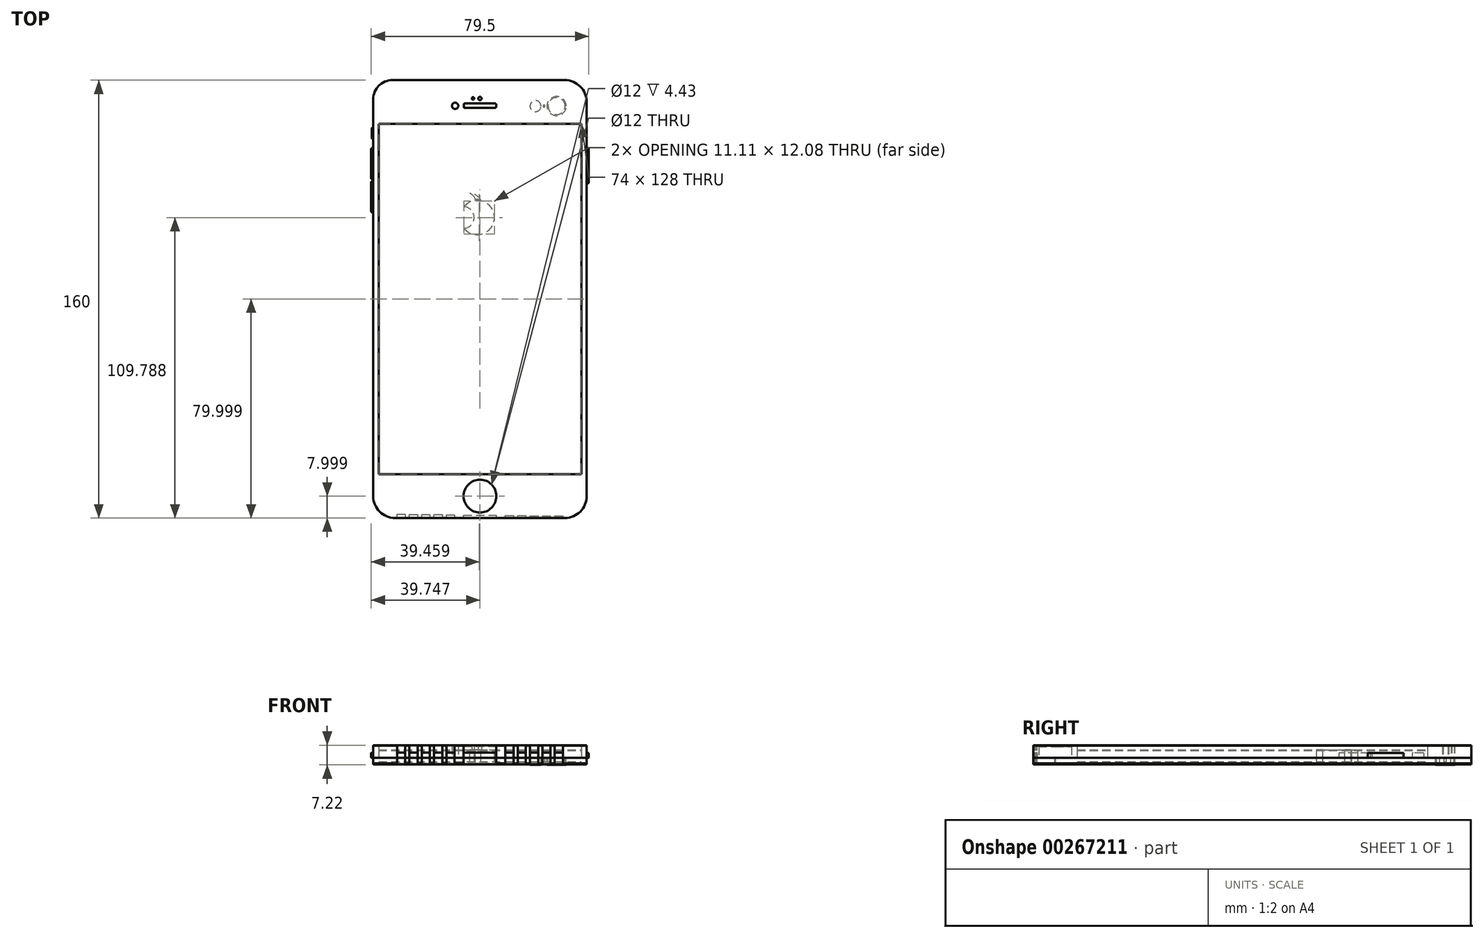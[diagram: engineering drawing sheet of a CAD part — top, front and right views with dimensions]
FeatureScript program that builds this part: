
annotation { "Feature Type Name" : "Feature", "Feature Type Description" : "" }
export const myFeature = defineFeature(function(context is Context, id is Id, definition is map)
    precondition{}
    {
        {
            var Q0;
            Q0=qCreatedBy(makeId("Top.planeOp"),FACE);
            var sketch = newSketch(context, id + "F0", { "sketchPlane" : qUnion([Q0])});
            skLineSegment(sketch, "E0", {"start": v(-50.56, 65.79) * mm, "end": v(-50.56, -79.21) * mm});
            skLineSegment(sketch, "E1", {"start": v(-42.56, -87.21) * mm, "end": v(19.44, -87.21) * mm});
            skLineSegment(sketch, "E2", {"start": v(27.44, -79.21) * mm, "end": v(27.44, 64.79) * mm});
            skLineSegment(sketch, "E3", {"start": v(19.44, 72.79) * mm, "end": v(-43.56, 72.79) * mm});
            skPoint(sketch, "E4.visualSharp", {"position": v(-50.56, 72.79) * mm});
            skArc(sketch, "E4.filletArc", {"start": v(-43.56, 72.79) * mm, "mid": v(-48.51, 70.74) * mm, "end": v(-50.56, 65.79) * mm});
            skPoint(sketch, "E5.visualSharp", {"position": v(27.44, 72.79) * mm});
            skArc(sketch, "E5.filletArc", {"start": v(27.44, 64.79) * mm, "mid": v(25.1, 70.45) * mm, "end": v(19.44, 72.79) * mm});
            skPoint(sketch, "E6.visualSharp", {"position": v(27.44, -87.21) * mm});
            skArc(sketch, "E6.filletArc", {"start": v(19.44, -87.21) * mm, "mid": v(25.1, -84.87) * mm, "end": v(27.44, -79.21) * mm});
            skPoint(sketch, "E7.visualSharp", {"position": v(-50.56, -87.21) * mm});
            skArc(sketch, "E7.filletArc", {"start": v(-50.56, -79.21) * mm, "mid": v(-48.22, -84.87) * mm, "end": v(-42.56, -87.21) * mm});
            skLineSegment(sketch, "E8", {"start": v(-48.56, -71.21) * mm, "end": v(25.44, -71.21) * mm});
            skCircle(sketch, "E9", {"center": v(-11.56, -79.21) * mm, "radius": 6 * mm});
            skLineSegment(sketch, "E10", {"start": v(-48.56, 56.79) * mm, "end": v(25.44, 56.79) * mm});
            skLineSegment(sketch, "E11", {"start": v(-17.49, 63.79) * mm, "end": v(-17.49, 63.1) * mm});
            skLineSegment(sketch, "E12", {"start": v(-16.99, 62.6) * mm, "end": v(-6.14, 62.6) * mm});
            skLineSegment(sketch, "E13", {"start": v(-5.64, 63.1) * mm, "end": v(-5.64, 63.79) * mm});
            skLineSegment(sketch, "E14", {"start": v(-6.14, 64.29) * mm, "end": v(-16.99, 64.29) * mm});
            skCircle(sketch, "E15", {"center": v(-20.64, 63.39) * mm, "radius": 1.15 * mm});
            skPoint(sketch, "E16.visualSharp", {"position": v(-5.64, 62.6) * mm});
            skArc(sketch, "E16.filletArc", {"start": v(-6.14, 62.6) * mm, "mid": v(-5.79, 62.74) * mm, "end": v(-5.64, 63.1) * mm});
            skPoint(sketch, "E17.visualSharp", {"position": v(-5.64, 64.29) * mm});
            skArc(sketch, "E17.filletArc", {"start": v(-5.64, 63.79) * mm, "mid": v(-5.79, 64.14) * mm, "end": v(-6.14, 64.29) * mm});
            skPoint(sketch, "E18.visualSharp", {"position": v(-17.49, 64.29) * mm});
            skArc(sketch, "E18.filletArc", {"start": v(-16.99, 64.29) * mm, "mid": v(-17.34, 64.14) * mm, "end": v(-17.49, 63.79) * mm});
            skPoint(sketch, "E19.visualSharp", {"position": v(-17.49, 62.6) * mm});
            skArc(sketch, "E19.filletArc", {"start": v(-17.49, 63.1) * mm, "mid": v(-17.34, 62.74) * mm, "end": v(-16.99, 62.6) * mm});
            skLineSegment(sketch, "E20", {"start": v(25.44, -71.21) * mm, "end": v(25.44, 56.79) * mm});
            skLineSegment(sketch, "E21", {"start": v(-48.56, 56.79) * mm, "end": v(-48.56, -71.21) * mm});
            skCircle(sketch, "E22", {"center": v(-14.11, 66.09) * mm, "radius": 0.45 * mm});
            skCircle(sketch, "E23", {"center": v(-11.56, 66.09) * mm, "radius": 0.6 * mm});
            skPoint(sketch, "E24.start.orphan", {"position": v(-17.49, 63.44) * mm});
            skPoint(sketch, "E25.center.orphan", {"position": v(9.63, 64.79) * mm});
            skPoint(sketch, "E26.center.orphan", {"position": v(4.38, 64.79) * mm});
            skPoint(sketch, "E27.center.orphan", {"position": v(15.68, 63.79) * mm});
            skPoint(sketch, "E28.center.orphan", {"position": v(4.32, 63.79) * mm});
            skPoint(sketch, "E29.center.orphan", {"position": v(8.95, 63.79) * mm});
            skCircle(sketch, "E30", {"center": v(16.44, 63.29) * mm, "radius": 3.5 * mm});
            skCircle(sketch, "E31", {"center": v(11.84, 63.29) * mm, "radius": 0.35 * mm});
            skCircle(sketch, "E32", {"center": v(8.74, 63.29) * mm, "radius": 2 * mm});
            skLineSegment(sketch, "E33", {"start": v(-50.56, 55.39) * mm, "end": v(-50.76, 55.39) * mm});
            skLineSegment(sketch, "E34", {"start": v(-51.06, 55.09) * mm, "end": v(-51.06, 51.59) * mm});
            skLineSegment(sketch, "E35", {"start": v(-50.76, 51.29) * mm, "end": v(-50.56, 51.29) * mm});
            skLineSegment(sketch, "E36", {"start": v(-50.56, 48.01) * mm, "end": v(-50.81, 48.01) * mm});
            skLineSegment(sketch, "E37", {"start": v(-51.31, 47.51) * mm, "end": v(-51.31, 37.01) * mm});
            skLineSegment(sketch, "E38", {"start": v(-50.81, 36.51) * mm, "end": v(-50.56, 36.51) * mm});
            skLineSegment(sketch, "E39", {"start": v(-50.56, 35.89) * mm, "end": v(-50.81, 35.89) * mm});
            skLineSegment(sketch, "E40", {"start": v(-51.31, 35.39) * mm, "end": v(-51.31, 24.89) * mm});
            skLineSegment(sketch, "E41", {"start": v(-50.81, 24.39) * mm, "end": v(-50.56, 24.39) * mm});
            skLineSegment(sketch, "E42", {"start": v(27.44, 48.01) * mm, "end": v(27.69, 48.01) * mm});
            skLineSegment(sketch, "E43", {"start": v(28.19, 47.51) * mm, "end": v(28.19, 35.51) * mm});
            skLineSegment(sketch, "E44", {"start": v(27.69, 35.01) * mm, "end": v(27.44, 35.01) * mm});
            skPoint(sketch, "E45.visualSharp", {"position": v(-51.31, 24.39) * mm});
            skArc(sketch, "E45.filletArc", {"start": v(-51.31, 24.89) * mm, "mid": v(-51.17, 24.54) * mm, "end": v(-50.81, 24.39) * mm});
            skPoint(sketch, "E46.visualSharp", {"position": v(-51.31, 35.89) * mm});
            skArc(sketch, "E46.filletArc", {"start": v(-50.81, 35.89) * mm, "mid": v(-51.17, 35.74) * mm, "end": v(-51.31, 35.39) * mm});
            skPoint(sketch, "E47.visualSharp", {"position": v(-51.31, 36.51) * mm});
            skArc(sketch, "E47.filletArc", {"start": v(-51.31, 37.01) * mm, "mid": v(-51.17, 36.66) * mm, "end": v(-50.81, 36.51) * mm});
            skPoint(sketch, "E48.visualSharp", {"position": v(-51.31, 48.01) * mm});
            skArc(sketch, "E48.filletArc", {"start": v(-50.81, 48.01) * mm, "mid": v(-51.17, 47.87) * mm, "end": v(-51.31, 47.51) * mm});
            skPoint(sketch, "E49.visualSharp", {"position": v(-51.06, 51.29) * mm});
            skArc(sketch, "E49.filletArc", {"start": v(-51.06, 51.59) * mm, "mid": v(-50.97, 51.37) * mm, "end": v(-50.76, 51.29) * mm});
            skPoint(sketch, "E50.visualSharp", {"position": v(-51.06, 55.39) * mm});
            skArc(sketch, "E50.filletArc", {"start": v(-50.76, 55.39) * mm, "mid": v(-50.97, 55.3) * mm, "end": v(-51.06, 55.09) * mm});
            skPoint(sketch, "E51.visualSharp", {"position": v(28.19, 48.01) * mm});
            skArc(sketch, "E51.filletArc", {"start": v(28.19, 47.51) * mm, "mid": v(28.04, 47.87) * mm, "end": v(27.69, 48.01) * mm});
            skPoint(sketch, "E52.visualSharp", {"position": v(28.19, 35.01) * mm});
            skArc(sketch, "E52.filletArc", {"start": v(27.69, 35.01) * mm, "mid": v(28.04, 35.16) * mm, "end": v(28.19, 35.51) * mm});
            skArc(sketch, "E53", {"start": v(-17.4, 18.6) * mm, "mid": v(-6.3, 22.58) * mm, "end": v(-17.4, 26.55) * mm});
            skPoint(sketch, "E54.center.orphan", {"position": v(-12.56, 33.45) * mm});
            skArc(sketch, "E55", {"start": v(-17.4, 18.6) * mm, "mid": v(-13.68, 22.58) * mm, "end": v(-17.4, 26.55) * mm});
            skArc(sketch, "E56", {"start": v(-11.22, 29.05) * mm, "mid": v(-12.2, 29.18) * mm, "end": v(-13.2, 29.15) * mm});
            skArc(sketch, "E57.trimOffspring", {"start": v(-13.2, 29.15) * mm, "mid": v(-14.01, 30.52) * mm, "end": v(-15.29, 31.46) * mm});
            skArc(sketch, "E58.trimOffspring", {"start": v(-11.22, 29.05) * mm, "mid": v(-12.98, 30.72) * mm, "end": v(-15.29, 31.46) * mm});
            skCircle(sketch, "E59", {"center": v(16.44, 63.29) * mm, "radius": 3.11 * mm});
            skLineSegment(sketch, "E60", {"start": v(-5.56, -79.13) * mm, "end": v(-5.56, -79.3) * mm});
            skLineSegment(sketch, "E61", {"start": v(-41.84, -87.21) * mm, "end": v(-41.84, -85.86) * mm});
            skLineSegment(sketch, "E62", {"start": v(-41.84, -85.86) * mm, "end": v(-38.84, -85.86) * mm});
            skLineSegment(sketch, "E63", {"start": v(-38.84, -85.86) * mm, "end": v(-38.84, -87.21) * mm});
            skLineSegment(sketch, "E64", {"start": v(-37.34, -87.21) * mm, "end": v(-37.34, -85.88) * mm});
            skLineSegment(sketch, "E65", {"start": v(-37.34, -85.88) * mm, "end": v(-34.34, -85.88) * mm});
            skLineSegment(sketch, "E66", {"start": v(-34.34, -85.88) * mm, "end": v(-34.34, -87.21) * mm});
            skLineSegment(sketch, "E67", {"start": v(-32.84, -87.21) * mm, "end": v(-32.84, -85.9) * mm});
            skLineSegment(sketch, "E68", {"start": v(-32.84, -85.9) * mm, "end": v(-29.84, -85.9) * mm});
            skLineSegment(sketch, "E69", {"start": v(-29.84, -85.9) * mm, "end": v(-29.84, -87.21) * mm});
            skLineSegment(sketch, "E70", {"start": v(-28.34, -87.21) * mm, "end": v(-28.34, -86) * mm});
            skLineSegment(sketch, "E71", {"start": v(-28.34, -86) * mm, "end": v(-25.34, -86) * mm});
            skLineSegment(sketch, "E72", {"start": v(-25.34, -86) * mm, "end": v(-25.34, -87.21) * mm});
            skLineSegment(sketch, "E73", {"start": v(-23.84, -87.21) * mm, "end": v(-23.84, -86.05) * mm});
            skLineSegment(sketch, "E74", {"start": v(-23.84, -86.05) * mm, "end": v(-20.84, -86.05) * mm});
            skLineSegment(sketch, "E75", {"start": v(-20.84, -86.05) * mm, "end": v(-20.84, -87.21) * mm});
            skLineSegment(sketch, "E76", {"start": v(-17.56, -87.21) * mm, "end": v(-17.56, -86.22) * mm});
            skLineSegment(sketch, "E77", {"start": v(-17.56, -86.22) * mm, "end": v(-5.56, -86.22) * mm});
            skLineSegment(sketch, "E78", {"start": v(-5.56, -86.22) * mm, "end": v(-5.56, -87.21) * mm});
            skLineSegment(sketch, "E79", {"start": v(-2.28, -87.21) * mm, "end": v(-2.28, -86.28) * mm});
            skLineSegment(sketch, "E80", {"start": v(-2.28, -86.28) * mm, "end": v(0.72, -86.28) * mm});
            skLineSegment(sketch, "E81", {"start": v(0.72, -86.28) * mm, "end": v(0.72, -87.21) * mm});
            skLineSegment(sketch, "E82", {"start": v(2.22, -87.21) * mm, "end": v(2.22, -86.36) * mm});
            skLineSegment(sketch, "E83", {"start": v(2.22, -86.36) * mm, "end": v(5.22, -86.36) * mm});
            skLineSegment(sketch, "E84", {"start": v(5.22, -86.36) * mm, "end": v(5.22, -87.21) * mm});
            skLineSegment(sketch, "E85", {"start": v(6.72, -87.21) * mm, "end": v(6.72, -86.4) * mm});
            skLineSegment(sketch, "E86", {"start": v(6.72, -86.4) * mm, "end": v(9.72, -86.4) * mm});
            skLineSegment(sketch, "E87", {"start": v(9.72, -86.4) * mm, "end": v(9.72, -87.21) * mm});
            skLineSegment(sketch, "E88", {"start": v(11.22, -87.21) * mm, "end": v(11.22, -86.46) * mm});
            skLineSegment(sketch, "E89", {"start": v(11.22, -86.46) * mm, "end": v(14.22, -86.46) * mm});
            skLineSegment(sketch, "E90", {"start": v(14.22, -86.46) * mm, "end": v(14.22, -87.21) * mm});
            skLineSegment(sketch, "E91", {"start": v(15.72, -87.21) * mm, "end": v(15.72, -86.51) * mm});
            skLineSegment(sketch, "E92", {"start": v(15.72, -86.51) * mm, "end": v(18.72, -86.51) * mm});
            skLineSegment(sketch, "E93", {"start": v(18.72, -86.51) * mm, "end": v(18.72, -87.21) * mm});
            skPoint(sketch, "E94.start.orphan", {"position": v(5.22, -88.02) * mm});
            skPoint(sketch, "E95.start.orphan", {"position": v(6.72, -88.02) * mm});
            skSolve(sketch);
        }
        {
            var Q0;
            Q0=makeQuery(id+"F0.imprint","IMPRINT",FACE,{"disambiguationData":[TD([[makeQuery(id+"F0.imprint","IMPRINT",EDGE,{"derivedFrom":sQuery(id+"F0.wireOp",EDGE,"E0")}),1.0]])]});
            var Q1;
            Q1=makeQuery(id+"F0.imprint","IMPRINT",FACE,{"disambiguationData":[TD([[makeQuery(id+"F0.imprint","IMPRINT",EDGE,{"derivedFrom":sQuery(id+"F0.wireOp",EDGE,"E11")}),1.0]])]});
            var Q2;
            Q2=makeQuery(id+"F0.imprint","IMPRINT",FACE,{"disambiguationData":[TD([[makeQuery(id+"F0.imprint","IMPRINT",EDGE,{"derivedFrom":sQuery(id+"F0.wireOp",EDGE,"E22")}),1.0]])]});
            var Q3;
            Q3=makeQuery(id+"F0.imprint","IMPRINT",FACE,{"disambiguationData":[TD([[makeQuery(id+"F0.imprint","IMPRINT",EDGE,{"derivedFrom":sQuery(id+"F0.wireOp",EDGE,"E23")}),1.0]])]});
            var Q4;
            Q4=makeQuery(id+"F0.imprint","IMPRINT",FACE,{"disambiguationData":[TD([[makeQuery(id+"F0.imprint","IMPRINT",EDGE,{"derivedFrom":sQuery(id+"F0.wireOp",EDGE,"E15")}),1.0]])]});
            var Q5;
            Q5=makeQuery(id+"F0.imprint","IMPRINT",FACE,{"disambiguationData":[TD([[makeQuery(id+"F0.imprint","IMPRINT",EDGE,{"derivedFrom":sQuery(id+"F0.wireOp",EDGE,"E9")}),1.0]])]});
            var Q6;
            Q6=makeQuery(id+"F0.imprint","IMPRINT",FACE,{"disambiguationData":[TD([[makeQuery(id+"F0.imprint","IMPRINT",EDGE,{"derivedFrom":sQuery(id+"F0.wireOp",EDGE,"E8")}),1.0]])]});
            extrude(context, id + "F1", {"entities" : qUnion([Q0, Q1, Q2, Q3, Q4, Q5, Q6]), "oppositeDirection" : true, "depth" : 2 * mm});
        }
        {
            var Q0;
            Q0=makeQuery(id+"F0.imprint","IMPRINT",FACE,{"disambiguationData":[TD([[makeQuery(id+"F0.imprint","IMPRINT",EDGE,{"derivedFrom":sQuery(id+"F0.wireOp",EDGE,"E0")}),1.0]])]});
            extrude(context, id + "F2", {"entities" : qUnion([Q0]), "depth" : 3.6 * mm});
        }
        {
            var Q0;
            Q0=makeQuery(id+"F0.imprint","IMPRINT",FACE,{"disambiguationData":[TD([[makeQuery(id+"F0.imprint","IMPRINT",EDGE,{"derivedFrom":sQuery(id+"F0.wireOp",EDGE,"E8")}),1.0]])]});
            extrude(context, id + "F3", {"entities" : qUnion([Q0]), "depth" : 2.88 * mm, "hasSecondDirection" : true, "secondDirectionOppositeDirection" : false, "secondDirectionDepth" : 0.14 * mm});
        }
        {
            var Q0;
            Q0=makeQuery(id+"F0.imprint","IMPRINT",FACE,{"disambiguationData":[TD([[makeQuery(id+"F0.imprint","IMPRINT",EDGE,{"derivedFrom":sQuery(id+"F0.wireOp",EDGE,"E8")}),1.0]])]});
            extrude(context, id + "F4", {"entities" : qUnion([Q0]), "operationType" : NewBodyOperationType.ADD, "depth" : 0.7 * mm});
        }
        {
            var Q0;
            Q0=makeQuery(id+"F0.imprint","IMPRINT",FACE,{"disambiguationData":[TD([[makeQuery(id+"F0.imprint","IMPRINT",EDGE,{"derivedFrom":sQuery(id+"F0.wireOp",EDGE,"E11")}),1.0]])]});
            var Q1;
            Q1=makeQuery(id+"F0.imprint","IMPRINT",FACE,{"disambiguationData":[TD([[makeQuery(id+"F0.imprint","IMPRINT",EDGE,{"derivedFrom":sQuery(id+"F0.wireOp",EDGE,"E15")}),1.0]])]});
            extrude(context, id + "F5", {"entities" : qUnion([Q0, Q1]), "depth" : 4.3 * mm});
        }
        {
            var Q0;
            Q0=makeQuery(id+"F0.imprint","IMPRINT",FACE,{"disambiguationData":[TD([[makeQuery(id+"F0.imprint","IMPRINT",EDGE,{"derivedFrom":sQuery(id+"F0.wireOp",EDGE,"E9")}),1.0]])]});
            extrude(context, id + "F6", {"entities" : qUnion([Q0]), "depth" : 4 * mm});
        }
        {
            var Q0;
            {var subQ0=sQuery(id+"F0.wireOp",EDGE,"E33");Q0=makeQuery(id+"F0.imprint","IMPRINT",FACE,{"disambiguationData":[TD([[makeQuery(id+"F0.imprint","IMPRINT",EDGE,{"derivedFrom":subQ0}),1.0]])]});}
            var Q1;
            {var subQ0=sQuery(id+"F0.wireOp",EDGE,"E36");Q1=makeQuery(id+"F0.imprint","IMPRINT",FACE,{"disambiguationData":[TD([[makeQuery(id+"F0.imprint","IMPRINT",EDGE,{"derivedFrom":subQ0}),1.0]])]});}
            var Q2;
            {var subQ0=sQuery(id+"F0.wireOp",EDGE,"E39");Q2=makeQuery(id+"F0.imprint","IMPRINT",FACE,{"disambiguationData":[TD([[makeQuery(id+"F0.imprint","IMPRINT",EDGE,{"derivedFrom":subQ0}),1.0]])]});}
            var Q3;
            {var subQ0=sQuery(id+"F0.wireOp",EDGE,"E42");Q3=makeQuery(id+"F0.imprint","IMPRINT",FACE,{"disambiguationData":[TD([[makeQuery(id+"F0.imprint","IMPRINT",EDGE,{"derivedFrom":subQ0}),-1.0]])]});}
            extrude(context, id + "F7", {"entities" : qUnion([Q0, Q1, Q2, Q3]), "depth" : 1.77 * mm});
        }
        {
            var Q0;
            Q0=makeQuery(id+"F0.imprint","IMPRINT",FACE,{"disambiguationData":[TD([[makeQuery(id+"F0.imprint","IMPRINT",EDGE,{"derivedFrom":sQuery(id+"F0.wireOp",EDGE,"E53")}),1.0]])]});
            var Q1;
            Q1=makeQuery(id+"F0.imprint","IMPRINT",FACE,{"disambiguationData":[TD([[makeQuery(id+"F0.imprint","IMPRINT",EDGE,{"derivedFrom":sQuery(id+"F0.wireOp",EDGE,"E56")}),-1.0]])]});
            extrude(context, id + "F8", {"entities" : qUnion([Q0, Q1]), "operationType" : NewBodyOperationType.ADD, "oppositeDirection" : true, "depth" : 0.17 * mm});
        }
        {
            var Q0;
            Q0=makeQuery(id+"F0.imprint","IMPRINT",FACE,{"disambiguationData":[TD([[makeQuery(id+"F0.imprint","IMPRINT",EDGE,{"derivedFrom":sQuery(id+"F0.wireOp",EDGE,"E59")}),1.0]])]});
            var Q1;
            Q1=makeQuery(id+"F0.imprint","IMPRINT",FACE,{"disambiguationData":[TD([[makeQuery(id+"F0.imprint","IMPRINT",EDGE,{"derivedFrom":sQuery(id+"F0.wireOp",EDGE,"E30")}),1.0]])]});
            extrude(context, id + "F9", {"entities" : qUnion([Q0, Q1]), "oppositeDirection" : true, "depth" : 2.2 * mm});
        }
        {
            var Q0;
            Q0=makeQuery(id+"F0.imprint","IMPRINT",FACE,{"disambiguationData":[TD([[makeQuery(id+"F0.imprint","IMPRINT",EDGE,{"derivedFrom":sQuery(id+"F0.wireOp",EDGE,"E8")}),1.0]])]});
            var Q1;
            Q1=makeQuery(id+"F0.imprint","IMPRINT",FACE,{"disambiguationData":[TD([[makeQuery(id+"F0.imprint","IMPRINT",EDGE,{"derivedFrom":sQuery(id+"F0.wireOp",EDGE,"E53")}),1.0]])]});
            var Q2;
            Q2=makeQuery(id+"F0.imprint","IMPRINT",FACE,{"disambiguationData":[TD([[makeQuery(id+"F0.imprint","IMPRINT",EDGE,{"derivedFrom":sQuery(id+"F0.wireOp",EDGE,"E56")}),-1.0]])]});
            extrude(context, id + "F10", {"entities" : qUnion([Q0, Q1, Q2]), "depth" : 2.6 * mm, "hasSecondDirection" : true, "secondDirectionOppositeDirection" : true, "secondDirectionDepth" : 1.4 * mm});
        }
        {
            var Q0;
            Q0=makeQuery(id+"F0.imprint","IMPRINT",FACE,{"disambiguationData":[TD([[makeQuery(id+"F0.imprint","IMPRINT",EDGE,{"derivedFrom":sQuery(id+"F0.wireOp",EDGE,"E8")}),1.0]])]});
            var Q1;
            Q1=makeQuery(id+"F0.imprint","IMPRINT",FACE,{"disambiguationData":[TD([[makeQuery(id+"F0.imprint","IMPRINT",EDGE,{"derivedFrom":sQuery(id+"F0.wireOp",EDGE,"E53")}),1.0]])]});
            var Q2;
            Q2=makeQuery(id+"F0.imprint","IMPRINT",FACE,{"disambiguationData":[TD([[makeQuery(id+"F0.imprint","IMPRINT",EDGE,{"derivedFrom":sQuery(id+"F0.wireOp",EDGE,"E56")}),-1.0]])]});
            extrude(context, id + "F11", {"entities" : qUnion([Q0, Q1, Q2]), "depth" : 4.6 * mm});
        }
        {
            var Q0;
            Q0=makeQuery(id+"F0.imprint","IMPRINT",FACE,{"disambiguationData":[TD([[makeQuery(id+"F0.imprint","IMPRINT",EDGE,{"derivedFrom":sQuery(id+"F0.wireOp",EDGE,"E30")}),1.0]])]});
            var Q1;
            Q1=makeQuery(id+"F0.imprint","IMPRINT",FACE,{"disambiguationData":[TD([[makeQuery(id+"F0.imprint","IMPRINT",EDGE,{"derivedFrom":sQuery(id+"F0.wireOp",EDGE,"E31")}),1.0]])]});
            var Q2;
            Q2=makeQuery(id+"F0.imprint","IMPRINT",FACE,{"disambiguationData":[TD([[makeQuery(id+"F0.imprint","IMPRINT",EDGE,{"derivedFrom":sQuery(id+"F0.wireOp",EDGE,"E32")}),1.0]])]});
            extrude(context, id + "F12", {"entities" : qUnion([Q0, Q1, Q2]), "oppositeDirection" : true, "depth" : 2.62 * mm});
        }
        {
            var Q0;
            Q0=makeQuery(id+"F0.imprint","IMPRINT",FACE,{"disambiguationData":[TD([[makeQuery(id+"F0.imprint","IMPRINT",EDGE,{"derivedFrom":sQuery(id+"F0.wireOp",EDGE,"E1")}),1.0]])]});
            var Q1;
            Q1=makeQuery(id+"F0.imprint","IMPRINT",FACE,{"disambiguationData":[TD([[makeQuery(id+"F0.imprint","IMPRINT",EDGE,{"derivedFrom":sQuery(id+"F0.wireOp",EDGE,"E30")}),1.0]])]});
            var Q2;
            Q2=makeQuery(id+"F0.imprint","IMPRINT",FACE,{"disambiguationData":[TD([[makeQuery(id+"F0.imprint","IMPRINT",EDGE,{"derivedFrom":sQuery(id+"F0.wireOp",EDGE,"E31")}),1.0]])]});
            var Q3;
            Q3=makeQuery(id+"F0.imprint","IMPRINT",FACE,{"disambiguationData":[TD([[makeQuery(id+"F0.imprint","IMPRINT",EDGE,{"derivedFrom":sQuery(id+"F0.wireOp",EDGE,"E32")}),1.0]])]});
            extrude(context, id + "F13", {"entities" : qUnion([Q0, Q1, Q2, Q3]), "depth" : 4.1 * mm});
        }
        {
            var Q0;
            Q0=makeQuery(id+"F0.imprint","IMPRINT",FACE,{"disambiguationData":[TD([[makeQuery(id+"F0.imprint","IMPRINT",EDGE,{"derivedFrom":sQuery(id+"F0.wireOp",EDGE,"E59")}),1.0]])]});
            var Q1;
            Q1=makeQuery(id+"F0.imprint","IMPRINT",FACE,{"disambiguationData":[TD([[makeQuery(id+"F0.imprint","IMPRINT",EDGE,{"derivedFrom":sQuery(id+"F0.wireOp",EDGE,"E30")}),1.0]])]});
            var Q2;
            Q2=makeQuery(id+"F0.imprint","IMPRINT",FACE,{"disambiguationData":[TD([[makeQuery(id+"F0.imprint","IMPRINT",EDGE,{"derivedFrom":sQuery(id+"F0.wireOp",EDGE,"E1")}),1.0]])]});
            var Q3;
            Q3=makeQuery(id+"F0.imprint","IMPRINT",FACE,{"disambiguationData":[TD([[makeQuery(id+"F0.imprint","IMPRINT",EDGE,{"derivedFrom":sQuery(id+"F0.wireOp",EDGE,"E32")}),1.0]])]});
            var Q4;
            Q4=makeQuery(id+"F0.imprint","IMPRINT",FACE,{"disambiguationData":[TD([[makeQuery(id+"F0.imprint","IMPRINT",EDGE,{"derivedFrom":sQuery(id+"F0.wireOp",EDGE,"E31")}),1.0]])]});
            extrude(context, id + "F14", {"entities" : qUnion([Q0, Q1, Q2, Q3, Q4]), "depth" : 4.43 * mm});
        }
        {
            var Q0;
            Q0=makeQuery(id+"F0.imprint","IMPRINT",FACE,{"disambiguationData":[TD([[makeQuery(id+"F0.imprint","IMPRINT",EDGE,{"derivedFrom":sQuery(id+"F0.wireOp",EDGE,"E23")}),1.0]])]});
            var Q1;
            Q1=makeQuery(id+"F0.imprint","IMPRINT",FACE,{"disambiguationData":[TD([[makeQuery(id+"F0.imprint","IMPRINT",EDGE,{"derivedFrom":sQuery(id+"F0.wireOp",EDGE,"E22")}),1.0]])]});
            extrude(context, id + "F15", {"entities" : qUnion([Q0, Q1]), "operationType" : NewBodyOperationType.ADD, "depth" : 4.42 * mm});
        }
        {
            var Q0;
            {var subQ0=sQuery(id+"F0.wireOp",EDGE,"E61");Q0=makeQuery(id+"F0.imprint","IMPRINT",FACE,{"disambiguationData":[TD([[makeQuery(id+"F0.imprint","IMPRINT",EDGE,{"derivedFrom":subQ0}),-1.0]])]});}
            var Q1;
            {var subQ0=sQuery(id+"F0.wireOp",EDGE,"E64");Q1=makeQuery(id+"F0.imprint","IMPRINT",FACE,{"disambiguationData":[TD([[makeQuery(id+"F0.imprint","IMPRINT",EDGE,{"derivedFrom":subQ0}),-1.0]])]});}
            var Q2;
            {var subQ0=sQuery(id+"F0.wireOp",EDGE,"E67");Q2=makeQuery(id+"F0.imprint","IMPRINT",FACE,{"disambiguationData":[TD([[makeQuery(id+"F0.imprint","IMPRINT",EDGE,{"derivedFrom":subQ0}),-1.0]])]});}
            var Q3;
            {var subQ0=sQuery(id+"F0.wireOp",EDGE,"E70");Q3=makeQuery(id+"F0.imprint","IMPRINT",FACE,{"disambiguationData":[TD([[makeQuery(id+"F0.imprint","IMPRINT",EDGE,{"derivedFrom":subQ0}),-1.0]])]});}
            var Q4;
            {var subQ0=sQuery(id+"F0.wireOp",EDGE,"E73");Q4=makeQuery(id+"F0.imprint","IMPRINT",FACE,{"disambiguationData":[TD([[makeQuery(id+"F0.imprint","IMPRINT",EDGE,{"derivedFrom":subQ0}),-1.0]])]});}
            var Q5;
            {var subQ0=sQuery(id+"F0.wireOp",EDGE,"E76");Q5=makeQuery(id+"F0.imprint","IMPRINT",FACE,{"disambiguationData":[TD([[makeQuery(id+"F0.imprint","IMPRINT",EDGE,{"derivedFrom":subQ0}),-1.0]])]});}
            var Q6;
            {var subQ0=sQuery(id+"F0.wireOp",EDGE,"E79");Q6=makeQuery(id+"F0.imprint","IMPRINT",FACE,{"disambiguationData":[TD([[makeQuery(id+"F0.imprint","IMPRINT",EDGE,{"derivedFrom":subQ0}),-1.0]])]});}
            var Q7;
            {var subQ0=sQuery(id+"F0.wireOp",EDGE,"E82");Q7=makeQuery(id+"F0.imprint","IMPRINT",FACE,{"disambiguationData":[TD([[makeQuery(id+"F0.imprint","IMPRINT",EDGE,{"derivedFrom":subQ0}),-1.0]])]});}
            var Q8;
            {var subQ0=sQuery(id+"F0.wireOp",EDGE,"E85");Q8=makeQuery(id+"F0.imprint","IMPRINT",FACE,{"disambiguationData":[TD([[makeQuery(id+"F0.imprint","IMPRINT",EDGE,{"derivedFrom":subQ0}),-1.0]])]});}
            var Q9;
            {var subQ0=sQuery(id+"F0.wireOp",EDGE,"E88");Q9=makeQuery(id+"F0.imprint","IMPRINT",FACE,{"disambiguationData":[TD([[makeQuery(id+"F0.imprint","IMPRINT",EDGE,{"derivedFrom":subQ0}),-1.0]])]});}
            var Q10;
            {var subQ0=sQuery(id+"F0.wireOp",EDGE,"E91");Q10=makeQuery(id+"F0.imprint","IMPRINT",FACE,{"disambiguationData":[TD([[makeQuery(id+"F0.imprint","IMPRINT",EDGE,{"derivedFrom":subQ0}),-1.0]])]});}
            extrude(context, id + "F16", {"entities" : qUnion([Q0, Q1, Q2, Q3, Q4, Q5, Q6, Q7, Q8, Q9, Q10]), "depth" : 1.9 * mm});
        }
        {
            var Q0;
            Q0=makeQuery(id+"F0.imprint","IMPRINT",FACE,{"disambiguationData":[TD([[makeQuery(id+"F0.imprint","IMPRINT",EDGE,{"derivedFrom":sQuery(id+"F0.wireOp",EDGE,"E3")}),1.0]])]});
            var Q1;
            {var subQ0=sQuery(id+"F0.wireOp",EDGE,"E61");Q1=makeQuery(id+"F0.imprint","IMPRINT",FACE,{"disambiguationData":[TD([[makeQuery(id+"F0.imprint","IMPRINT",EDGE,{"derivedFrom":subQ0}),-1.0]])]});}
            var Q2;
            {var subQ0=sQuery(id+"F0.wireOp",EDGE,"E64");Q2=makeQuery(id+"F0.imprint","IMPRINT",FACE,{"disambiguationData":[TD([[makeQuery(id+"F0.imprint","IMPRINT",EDGE,{"derivedFrom":subQ0}),-1.0]])]});}
            var Q3;
            {var subQ0=sQuery(id+"F0.wireOp",EDGE,"E67");Q3=makeQuery(id+"F0.imprint","IMPRINT",FACE,{"disambiguationData":[TD([[makeQuery(id+"F0.imprint","IMPRINT",EDGE,{"derivedFrom":subQ0}),-1.0]])]});}
            var Q4;
            {var subQ0=sQuery(id+"F0.wireOp",EDGE,"E70");Q4=makeQuery(id+"F0.imprint","IMPRINT",FACE,{"disambiguationData":[TD([[makeQuery(id+"F0.imprint","IMPRINT",EDGE,{"derivedFrom":subQ0}),-1.0]])]});}
            var Q5;
            {var subQ0=sQuery(id+"F0.wireOp",EDGE,"E73");Q5=makeQuery(id+"F0.imprint","IMPRINT",FACE,{"disambiguationData":[TD([[makeQuery(id+"F0.imprint","IMPRINT",EDGE,{"derivedFrom":subQ0}),-1.0]])]});}
            var Q6;
            {var subQ0=sQuery(id+"F0.wireOp",EDGE,"E76");Q6=makeQuery(id+"F0.imprint","IMPRINT",FACE,{"disambiguationData":[TD([[makeQuery(id+"F0.imprint","IMPRINT",EDGE,{"derivedFrom":subQ0}),-1.0]])]});}
            var Q7;
            {var subQ0=sQuery(id+"F0.wireOp",EDGE,"E79");Q7=makeQuery(id+"F0.imprint","IMPRINT",FACE,{"disambiguationData":[TD([[makeQuery(id+"F0.imprint","IMPRINT",EDGE,{"derivedFrom":subQ0}),-1.0]])]});}
            var Q8;
            {var subQ0=sQuery(id+"F0.wireOp",EDGE,"E82");Q8=makeQuery(id+"F0.imprint","IMPRINT",FACE,{"disambiguationData":[TD([[makeQuery(id+"F0.imprint","IMPRINT",EDGE,{"derivedFrom":subQ0}),-1.0]])]});}
            var Q9;
            {var subQ0=sQuery(id+"F0.wireOp",EDGE,"E85");Q9=makeQuery(id+"F0.imprint","IMPRINT",FACE,{"disambiguationData":[TD([[makeQuery(id+"F0.imprint","IMPRINT",EDGE,{"derivedFrom":subQ0}),-1.0]])]});}
            var Q10;
            {var subQ0=sQuery(id+"F0.wireOp",EDGE,"E91");Q10=makeQuery(id+"F0.imprint","IMPRINT",FACE,{"disambiguationData":[TD([[makeQuery(id+"F0.imprint","IMPRINT",EDGE,{"derivedFrom":subQ0}),-1.0]])]});}
            var Q11;
            {var subQ0=sQuery(id+"F0.wireOp",EDGE,"E88");Q11=makeQuery(id+"F0.imprint","IMPRINT",FACE,{"disambiguationData":[TD([[makeQuery(id+"F0.imprint","IMPRINT",EDGE,{"derivedFrom":subQ0}),-1.0]])]});}
            var Q12;
            Q12=makeQuery(id+"F0.imprint","IMPRINT",FACE,{"disambiguationData":[TD([[makeQuery(id+"F0.imprint","IMPRINT",EDGE,{"derivedFrom":sQuery(id+"F0.wireOp",EDGE,"E59")}),1.0]])]});
            var Q13;
            Q13=makeQuery(id+"F0.imprint","IMPRINT",FACE,{"disambiguationData":[TD([[makeQuery(id+"F0.imprint","IMPRINT",EDGE,{"derivedFrom":sQuery(id+"F0.wireOp",EDGE,"E32")}),1.0]])]});
            var Q14;
            Q14=makeQuery(id+"F0.imprint","IMPRINT",FACE,{"disambiguationData":[TD([[makeQuery(id+"F0.imprint","IMPRINT",EDGE,{"derivedFrom":sQuery(id+"F0.wireOp",EDGE,"E31")}),1.0]])]});
            var Q15;
            Q15=makeQuery(id+"F0.imprint","IMPRINT",FACE,{"disambiguationData":[TD([[makeQuery(id+"F0.imprint","IMPRINT",EDGE,{"derivedFrom":sQuery(id+"F0.wireOp",EDGE,"E30")}),1.0]])]});
            extrude(context, id + "F17", {"entities" : qUnion([Q0, Q1, Q2, Q3, Q4, Q5, Q6, Q7, Q8, Q9, Q10, Q11, Q12, Q13, Q14, Q15]), "depth" : 4.6 * mm});
        }
        {
            var Q0;
            Q0=makeQuery(id+"F0.imprint","IMPRINT",FACE,{"disambiguationData":[TD([[makeQuery(id+"F0.imprint","IMPRINT",EDGE,{"derivedFrom":sQuery(id+"F0.wireOp",EDGE,"E3")}),1.0]])]});
            var Q1;
            {var subQ0=sQuery(id+"F0.wireOp",EDGE,"E91");Q1=makeQuery(id+"F0.imprint","IMPRINT",FACE,{"disambiguationData":[TD([[makeQuery(id+"F0.imprint","IMPRINT",EDGE,{"derivedFrom":subQ0}),-1.0]])]});}
            var Q2;
            {var subQ0=sQuery(id+"F0.wireOp",EDGE,"E88");Q2=makeQuery(id+"F0.imprint","IMPRINT",FACE,{"disambiguationData":[TD([[makeQuery(id+"F0.imprint","IMPRINT",EDGE,{"derivedFrom":subQ0}),-1.0]])]});}
            var Q3;
            {var subQ0=sQuery(id+"F0.wireOp",EDGE,"E85");Q3=makeQuery(id+"F0.imprint","IMPRINT",FACE,{"disambiguationData":[TD([[makeQuery(id+"F0.imprint","IMPRINT",EDGE,{"derivedFrom":subQ0}),-1.0]])]});}
            var Q4;
            {var subQ0=sQuery(id+"F0.wireOp",EDGE,"E82");Q4=makeQuery(id+"F0.imprint","IMPRINT",FACE,{"disambiguationData":[TD([[makeQuery(id+"F0.imprint","IMPRINT",EDGE,{"derivedFrom":subQ0}),-1.0]])]});}
            var Q5;
            {var subQ0=sQuery(id+"F0.wireOp",EDGE,"E79");Q5=makeQuery(id+"F0.imprint","IMPRINT",FACE,{"disambiguationData":[TD([[makeQuery(id+"F0.imprint","IMPRINT",EDGE,{"derivedFrom":subQ0}),-1.0]])]});}
            var Q6;
            {var subQ0=sQuery(id+"F0.wireOp",EDGE,"E76");Q6=makeQuery(id+"F0.imprint","IMPRINT",FACE,{"disambiguationData":[TD([[makeQuery(id+"F0.imprint","IMPRINT",EDGE,{"derivedFrom":subQ0}),-1.0]])]});}
            var Q7;
            {var subQ0=sQuery(id+"F0.wireOp",EDGE,"E60");Q7=makeQuery(id+"F0.imprint","IMPRINT",FACE,{"disambiguationData":[TD([[makeQuery(id+"F0.imprint","IMPRINT",EDGE,{"derivedFrom":subQ0}),-1.0]])]});}
            var Q8;
            {var subQ0=sQuery(id+"F0.wireOp",EDGE,"E73");Q8=makeQuery(id+"F0.imprint","IMPRINT",FACE,{"disambiguationData":[TD([[makeQuery(id+"F0.imprint","IMPRINT",EDGE,{"derivedFrom":subQ0}),-1.0]])]});}
            var Q9;
            {var subQ0=sQuery(id+"F0.wireOp",EDGE,"E70");Q9=makeQuery(id+"F0.imprint","IMPRINT",FACE,{"disambiguationData":[TD([[makeQuery(id+"F0.imprint","IMPRINT",EDGE,{"derivedFrom":subQ0}),-1.0]])]});}
            var Q10;
            {var subQ0=sQuery(id+"F0.wireOp",EDGE,"E67");Q10=makeQuery(id+"F0.imprint","IMPRINT",FACE,{"disambiguationData":[TD([[makeQuery(id+"F0.imprint","IMPRINT",EDGE,{"derivedFrom":subQ0}),-1.0]])]});}
            var Q11;
            {var subQ0=sQuery(id+"F0.wireOp",EDGE,"E61");Q11=makeQuery(id+"F0.imprint","IMPRINT",FACE,{"disambiguationData":[TD([[makeQuery(id+"F0.imprint","IMPRINT",EDGE,{"derivedFrom":subQ0}),-1.0]])]});}
            var Q12;
            {var subQ0=sQuery(id+"F0.wireOp",EDGE,"E64");Q12=makeQuery(id+"F0.imprint","IMPRINT",FACE,{"disambiguationData":[TD([[makeQuery(id+"F0.imprint","IMPRINT",EDGE,{"derivedFrom":subQ0}),-1.0]])]});}
            var Q13;
            Q13=makeQuery(id+"F0.imprint","IMPRINT",FACE,{"disambiguationData":[TD([[makeQuery(id+"F0.imprint","IMPRINT",EDGE,{"derivedFrom":sQuery(id+"F0.wireOp",EDGE,"E8")}),1.0]])]});
            var Q14;
            Q14=makeQuery(id+"F0.imprint","IMPRINT",FACE,{"disambiguationData":[TD([[makeQuery(id+"F0.imprint","IMPRINT",EDGE,{"derivedFrom":sQuery(id+"F0.wireOp",EDGE,"E11")}),1.0]])]});
            var Q15;
            Q15=makeQuery(id+"F0.imprint","IMPRINT",FACE,{"disambiguationData":[TD([[makeQuery(id+"F0.imprint","IMPRINT",EDGE,{"derivedFrom":sQuery(id+"F0.wireOp",EDGE,"E15")}),1.0]])]});
            var Q16;
            Q16=makeQuery(id+"F0.imprint","IMPRINT",FACE,{"disambiguationData":[TD([[makeQuery(id+"F0.imprint","IMPRINT",EDGE,{"derivedFrom":sQuery(id+"F0.wireOp",EDGE,"E22")}),1.0]])]});
            var Q17;
            Q17=makeQuery(id+"F0.imprint","IMPRINT",FACE,{"disambiguationData":[TD([[makeQuery(id+"F0.imprint","IMPRINT",EDGE,{"derivedFrom":sQuery(id+"F0.wireOp",EDGE,"E23")}),1.0]])]});
            extrude(context, id + "F18", {"entities" : qUnion([Q0, Q1, Q2, Q3, Q4, Q5, Q6, Q7, Q8, Q9, Q10, Q11, Q12, Q13, Q14, Q15, Q16, Q17]), "oppositeDirection" : true, "depth" : 2.5 * mm});
        }
        {
            var Q0;
            Q0=makeQuery(id+"F12.opExtrude","SWEPT_BODY",BODY,{"disambiguationData":[OSD([sQuery(id+"F0.wireOp",EDGE,"E31")])]});
            deleteBodies(context, id + "F19", {"entities" : qUnion([Q0])});
        }
        {
            var Q0;
            Q0=makeQuery(id+"F0.imprint","IMPRINT",FACE,{"disambiguationData":[TD([[makeQuery(id+"F0.imprint","IMPRINT",EDGE,{"derivedFrom":sQuery(id+"F0.wireOp",EDGE,"E31")}),1.0]])]});
            extrude(context, id + "F20", {"entities" : qUnion([Q0]), "oppositeDirection" : true, "depth" : 1.7 * mm});
        }
    });
